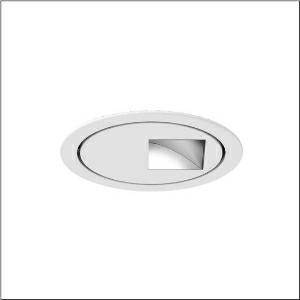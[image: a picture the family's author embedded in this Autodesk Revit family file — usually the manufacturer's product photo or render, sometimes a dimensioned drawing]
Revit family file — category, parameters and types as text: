
# Revit family: lunis_11_mini_round_51dk11b72wg21
name_source: partatom
category: Lighting Fixtures
units: mm (PartAtom-declared; Revit-internal decimal feet)

## family parameters
Cut with Voids When Loaded = No
Host = Face
Light Source = No
Part Type = Normal
Room Calculation Point = No
Round Connector Dimension = Use Diameter
Shared = No

## types (1)
- Lunis 11 mini round (1 x LED 4000K / CRI = 80 (unbekannt), 2470 lm, 4000K)
    Apparent Load = 28 VA
    CIE Flux Codes = 44 77 97 100 100
    Color Rendering = 80
    Color Temperature = 4000K
    Default Elevation = 1800 mm
    Description = Lunis 11 mini round, downlight, light control with wallwasher, of highly reflective aluminium, highly specular, light emission: direct distribution, LED rated luminous flux: 2.470lm, light colour: 840, control gear: ECG, with terminal, 3-pole, mains connection: 220..230V, AC/DC, 0/50..60Hz, LED module, luminaire module, of aluminium, highly specular, white, diameter: 176mm, clamping range: 1..40mm, recessing ring, of plastic, traffic white (RAL 9016), protection rating (complete): IP20, insulation class (complete): insulation class II (safety insulation), certification: CE, permissible ambient temperature for indoor applications: 0..+35°C, packaging unit: 1 piece
    Height = 0 mm  [stored 0 ft]
    Lamp = 1 x LED 4000K / CRI >= 80 (unbekannt)
    Lamp Light Flux = 2470 lm
    Lamp count = 1
    Length = 176 mm
    Luminous efficacy = 88 lm/W
    Manufacturer = Siteco
    ModVariant = No
    Model = 51DK11B72WG21
    Mounting Place = Ceiling
    Mounting Type = Recessed
    Number of Poles = 1
    OnlyDefault = Yes
    Power Factor = 1
    Product Name = Lunis 11 mini round
    Product group = downlight
    ProductGroupID = 401
    Protection Class = Protection class II
    Protection Degree = IP 20
    RLX_Detail_Level = 1
    RLX_Emergency_Light_Flux = 0 lm
    RLX_Emergency_Type = 0
    RLX_Emergency_Type_DB = No
    RlxData = <blob elided: 59329 chars, md5=01b141ec>
    Socket = socket
    Standby Power = 0 W
    System Light Flux = 2470 lm
    System Power = 28 W
    Type Comments = Product without accessories
    Type Image = l_1004772.jpg
    URL = http://relux.com
    VarID = ---
    Voltage = 0 V
    Weight = 0.00 kg
    Width = 176 mm

note: [stored X ft] marks values corroborated as IEEE doubles in the binary element streams (Revit-internal decimal feet)

## geometry (parser evidence)
native form markers: Blend x4, Sweep x11
no freeform markers — native parametric forms only
